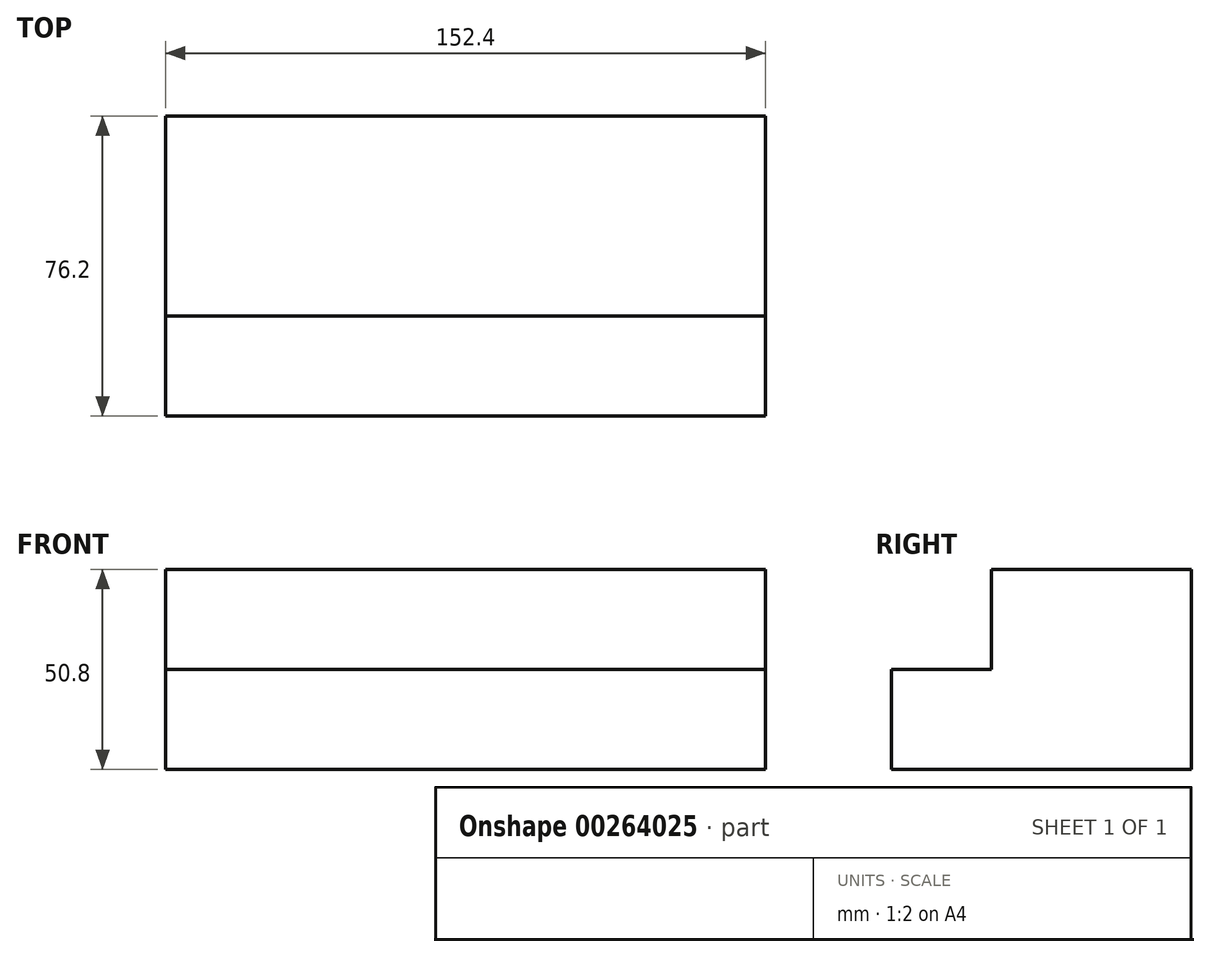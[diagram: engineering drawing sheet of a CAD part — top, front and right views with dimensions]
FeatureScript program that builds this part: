
annotation { "Feature Type Name" : "Feature", "Feature Type Description" : "" }
export const myFeature = defineFeature(function(context is Context, id is Id, definition is map)
    precondition{}
    {
        {
            var Q0;
            Q0=qCreatedBy(makeId("Right.planeOp"),FACE);
            var sketch = newSketch(context, id + "F0", { "sketchPlane" : qUnion([Q0])});
            skLineSegment(sketch, "E0", {"start": v(0, 0) * mm, "end": v(76.2, 0) * mm});
            skLineSegment(sketch, "E1", {"start": v(76.2, 0) * mm, "end": v(76.2, 50.8) * mm});
            skLineSegment(sketch, "E2", {"start": v(76.2, 50.8) * mm, "end": v(25.4, 50.8) * mm});
            skLineSegment(sketch, "E3", {"start": v(25.4, 25.4) * mm, "end": v(25.4, 50.8) * mm});
            skLineSegment(sketch, "E4", {"start": v(25.4, 25.4) * mm, "end": v(0, 25.4) * mm});
            skLineSegment(sketch, "E5", {"start": v(0, 25.4) * mm, "end": v(0, 0) * mm});
            skSolve(sketch);
        }
        {
            var Q0;
            Q0=makeQuery(id+"F0.imprint","IMPRINT",FACE,{"disambiguationData":[TD([[makeQuery(id+"F0.imprint","IMPRINT",EDGE,{"derivedFrom":sQuery(id+"F0.wireOp",EDGE,"E0")}),1.0]])]});
            extrude(context, id + "F1", {"entities" : qUnion([Q0]), "depth" : 152.4 * mm});
        }
    });
